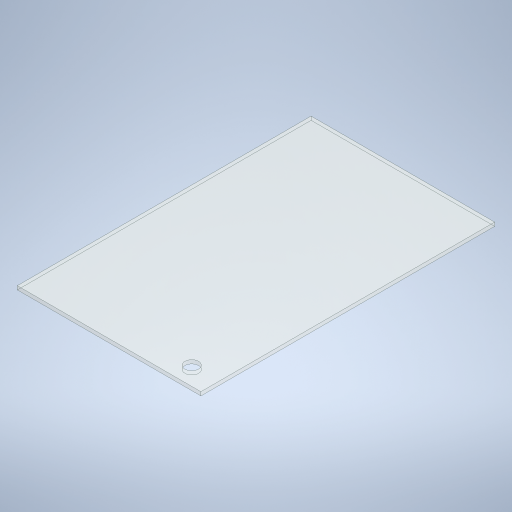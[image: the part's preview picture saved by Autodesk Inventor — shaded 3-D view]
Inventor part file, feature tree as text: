
AUTODESK INVENTOR PART (.ipt)
format: ipt  version: 2023 (Build 270158000, 158)  size: 297,472 bytes
history: native  units: in
note: dims shown in document units (in); Inventor stores cm internally (conversion verified against a paired STEP export)
features: extrude x2, sketch x2
ambient origin geometry x8: Origin, YZ Plane, XZ Plane, XY Plane, X Axis, Y Axis, Z Axis, Center Point
bodies: Solid1 (feature_tree)
feature tree (4):
  extrude  "Extrusion1"  Depth=54.0in
  extrude  "Extrusion2"  Depth=0.2in
  sketch  "Sketch1"  dims[d0=54.0in d1=54.0in]
  sketch  "Sketch2"  dims[d2=1.0in d3=1.0in d4=8.0in d5=16.0in d6=8.0in d7=16.0in d8=16.0in d9=8.0in d10=16.0in d11=8.0in d12=4.0in d13=4.0in d14=4.0in d15=4.0in d16=17.0in d17=17.0in d18=17.0in d19=17.0in d20=20.0in d21=1.0in d22=1.0in d23=1.0in d24=1.0in d25=45.0deg d26=2.5in d27=45.0deg d28=45.0deg d29=45.0deg d30=1.0in d31=1.0in d32=1.0in d33=1.0in d34=0.25in d35=0.25in d36=0.25in d37=0.25in d38=0.25in d39=0.25in d40=0.25in d41=0.25in d42=0.2in d43=0.0in d47=0.75in d48=1.5in d49=1.0in d50=1.0in d51=0.0in]
